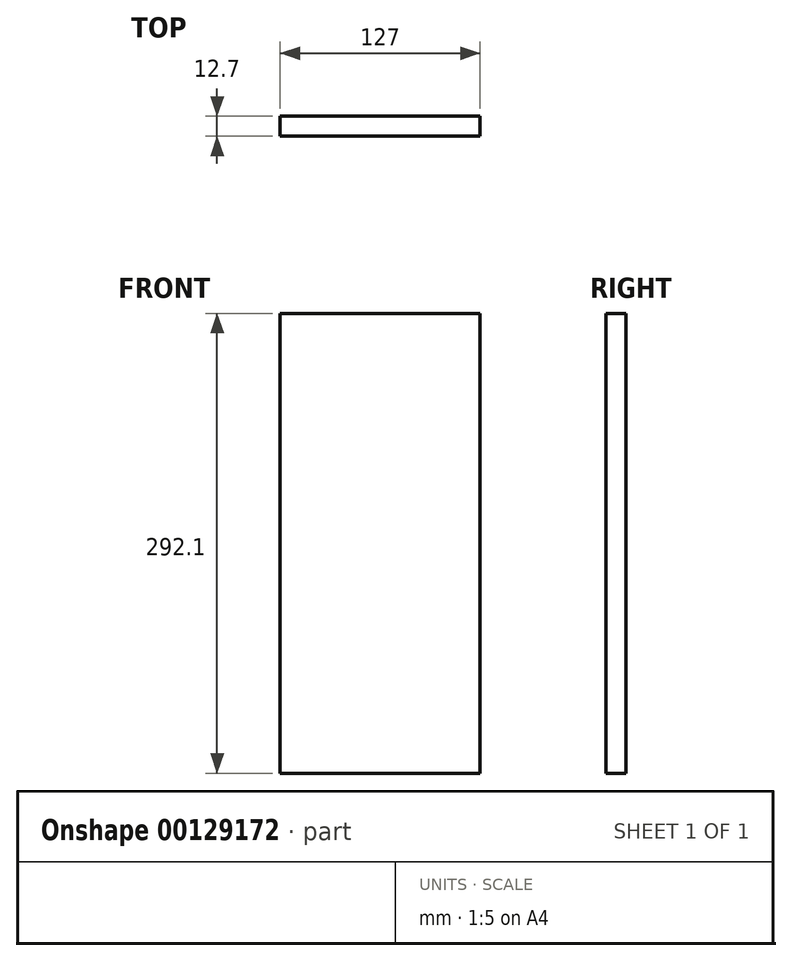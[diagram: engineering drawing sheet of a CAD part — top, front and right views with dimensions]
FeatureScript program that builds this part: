
annotation { "Feature Type Name" : "Feature", "Feature Type Description" : "" }
export const myFeature = defineFeature(function(context is Context, id is Id, definition is map)
    precondition{}
    {
        {
            var Q0;
            Q0=qCreatedBy(makeId("Front.planeOp"),FACE);
            var sketch = newSketch(context, id + "F0", { "sketchPlane" : qUnion([Q0])});
            skLineSegment(sketch, "E0.bottom", {"start": v(-63.5, 146.05) * mm, "end": v(63.5, 146.05) * mm});
            skLineSegment(sketch, "E0.top", {"start": v(-63.5, -146.05) * mm, "end": v(63.5, -146.05) * mm});
            skLineSegment(sketch, "E0.left", {"start": v(-63.5, 146.05) * mm, "end": v(-63.5, -146.05) * mm});
            skLineSegment(sketch, "E0.right", {"start": v(63.5, 146.05) * mm, "end": v(63.5, -146.05) * mm});
            skPoint(sketch, "E0.middle", {"position": v(0, 0) * mm});
            skSolve(sketch);
        }
        {
            var Q0;
            Q0 = qSketchRegion(id + "F0", true);
            extrude(context, id + "F1", {"entities" : qUnion([Q0]), "depth" : 12.7 * mm});
        }
    });
